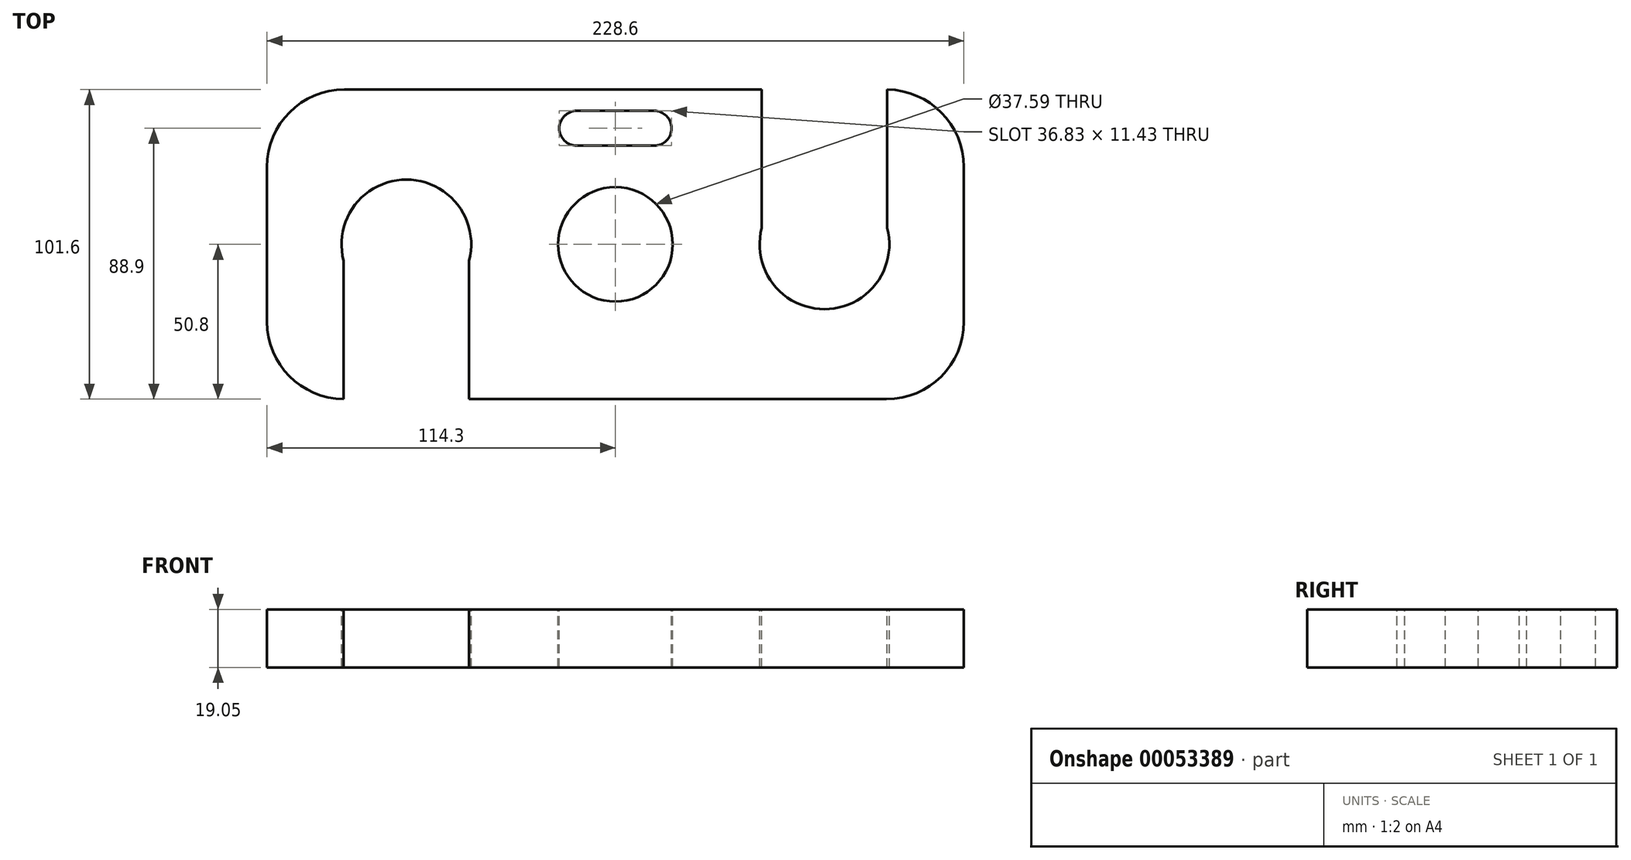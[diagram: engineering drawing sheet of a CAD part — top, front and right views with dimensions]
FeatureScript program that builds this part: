
annotation { "Feature Type Name" : "Feature", "Feature Type Description" : "" }
export const myFeature = defineFeature(function(context is Context, id is Id, definition is map)
    precondition{}
    {
        {
            var Q0;
            Q0=qCreatedBy(makeId("Top.planeOp"),FACE);
            var sketch = newSketch(context, id + "F0", { "sketchPlane" : qUnion([Q0])});
            skLineSegment(sketch, "E0.rect.bottom", {"start": v(88.9, 50.8) * mm, "end": v(-88.9, 50.8) * mm});
            skLineSegment(sketch, "E0.rect.top", {"start": v(88.9, -50.8) * mm, "end": v(-88.9, -50.8) * mm});
            skLineSegment(sketch, "E0.rect.left", {"start": v(114.3, 25.4) * mm, "end": v(114.3, -25.4) * mm});
            skLineSegment(sketch, "E0.rect.right", {"start": v(-114.3, 25.4) * mm, "end": v(-114.3, -25.4) * mm});
            skPoint(sketch, "E0.rect.middle", {"position": v(0, 0) * mm});
            skPoint(sketch, "E1.visualSharp", {"position": v(-114.3, 50.8) * mm});
            skArc(sketch, "E1.filletArc", {"start": v(-88.9, 50.8) * mm, "mid": v(-106.86, 43.36) * mm, "end": v(-114.3, 25.4) * mm});
            skPoint(sketch, "E2.visualSharp", {"position": v(-114.3, -50.8) * mm});
            skArc(sketch, "E2.filletArc", {"start": v(-114.3, -25.4) * mm, "mid": v(-106.86, -43.36) * mm, "end": v(-88.9, -50.8) * mm});
            skPoint(sketch, "E3.visualSharp", {"position": v(114.3, -50.8) * mm});
            skArc(sketch, "E3.filletArc", {"start": v(88.9, -50.8) * mm, "mid": v(106.86, -43.36) * mm, "end": v(114.3, -25.4) * mm});
            skPoint(sketch, "E4.visualSharp", {"position": v(114.3, 50.8) * mm});
            skArc(sketch, "E4.filletArc", {"start": v(114.3, 25.4) * mm, "mid": v(106.86, 43.36) * mm, "end": v(88.9, 50.8) * mm});
            skSolve(sketch);
        }
        {
            var Q0;
            Q0=makeQuery(id+"F0.imprint","IMPRINT",FACE,{"disambiguationData":[TD([[makeQuery(id+"F0.imprint","IMPRINT",EDGE,{"derivedFrom":sQuery(id+"F0.wireOp",EDGE,"E0.rect.bottom")}),1.0]])]});
            extrude(context, id + "F1", {"entities" : qUnion([Q0]), "depth" : 19.05 * mm});
        }
        {
            var Q0;
            Q0=makeQuery(id+"F1.opExtrude","CAP_FACE",FACE,{"disambiguationData":[OSD([sQuery(id+"F0.wireOp",EDGE,"E0.rect.bottom"),sQuery(id+"F0.wireOp",EDGE,"E0.rect.top"),sQuery(id+"F0.wireOp",EDGE,"E0.rect.left"),sQuery(id+"F0.wireOp",EDGE,"E0.rect.right"),sQuery(id+"F0.wireOp",EDGE,"E1.filletArc"),sQuery(id+"F0.wireOp",EDGE,"E2.filletArc"),sQuery(id+"F0.wireOp",EDGE,"E3.filletArc"),sQuery(id+"F0.wireOp",EDGE,"E4.filletArc")])],"isStart":false});
            var sketch = newSketch(context, id + "F2", { "sketchPlane" : qUnion([Q0])});
            skCircle(sketch, "E5", {"center": v(0, 0) * mm, "radius": 18.8 * mm});
            skSolve(sketch);
        }
        {
            var Q0;
            Q0=qSketchRegion(id+"F2",true);
            extrude(context, id + "F3", {"entities" : qUnion([Q0]), "operationType" : NewBodyOperationType.REMOVE, "endBound" : BoundingType.THROUGH_ALL, "oppositeDirection" : true, "depth" : 25.4 * mm});
        }
        {
            var Q0;
            Q0=makeQuery(id+"F1.opExtrude","CAP_FACE",FACE,{"disambiguationData":[OSD([sQuery(id+"F0.wireOp",EDGE,"E0.rect.bottom"),sQuery(id+"F0.wireOp",EDGE,"E0.rect.top"),sQuery(id+"F0.wireOp",EDGE,"E0.rect.left"),sQuery(id+"F0.wireOp",EDGE,"E0.rect.right"),sQuery(id+"F0.wireOp",EDGE,"E1.filletArc"),sQuery(id+"F0.wireOp",EDGE,"E2.filletArc"),sQuery(id+"F0.wireOp",EDGE,"E3.filletArc"),sQuery(id+"F0.wireOp",EDGE,"E4.filletArc")])],"isStart":false});
            var sketch = newSketch(context, id + "F4", { "sketchPlane" : qUnion([Q0])});
            skArc(sketch, "E6", {"start": v(-48, -5.4) * mm, "mid": v(-68.58, 21.27) * mm, "end": v(-89.15, -5.4) * mm});
            skArc(sketch, "E7.MirrorC", {"start": v(89.15, 5.4) * mm, "mid": v(68.58, -21.27) * mm, "end": v(48, 5.4) * mm});
            skLineSegment(sketch, "E8", {"start": v(-89.15, -50.8) * mm, "end": v(-89.15, -5.4) * mm});
            skLineSegment(sketch, "E9", {"start": v(-48, -50.8) * mm, "end": v(-48, -5.4) * mm});
            skLineSegment(sketch, "E10", {"start": v(89.15, 50.8) * mm, "end": v(89.15, 5.4) * mm});
            skLineSegment(sketch, "E11", {"start": v(48, 50.8) * mm, "end": v(48, 5.4) * mm});
            skLineSegment(sketch, "E12", {"start": v(-89.15, -50.8) * mm, "end": v(-48, -50.8) * mm});
            skLineSegment(sketch, "E13", {"start": v(48, 50.8) * mm, "end": v(89.15, 50.8) * mm});
            skLineSegment(sketch, "E14", {"start": v(-89.15, -5.4) * mm, "end": v(-48, -5.4) * mm, "construction": true});
            skLineSegment(sketch, "E15", {"start": v(48, 5.4) * mm, "end": v(89.15, 5.4) * mm, "construction": true});
            skSolve(sketch);
        }
        {
            var Q0;
            Q0=qSketchRegion(id+"F4",true);
            extrude(context, id + "F5", {"entities" : qUnion([Q0]), "operationType" : NewBodyOperationType.REMOVE, "endBound" : BoundingType.THROUGH_ALL, "oppositeDirection" : true, "depth" : 25.4 * mm});
        }
        {
            var Q0;
            Q0=makeQuery(id+"F1.opExtrude","CAP_FACE",FACE,{"disambiguationData":[OSD([sQuery(id+"F0.wireOp",EDGE,"E0.rect.bottom"),sQuery(id+"F0.wireOp",EDGE,"E0.rect.top"),sQuery(id+"F0.wireOp",EDGE,"E0.rect.left"),sQuery(id+"F0.wireOp",EDGE,"E0.rect.right"),sQuery(id+"F0.wireOp",EDGE,"E1.filletArc"),sQuery(id+"F0.wireOp",EDGE,"E2.filletArc"),sQuery(id+"F0.wireOp",EDGE,"E3.filletArc"),sQuery(id+"F0.wireOp",EDGE,"E4.filletArc")])],"isStart":false});
            var sketch = newSketch(context, id + "F6", { "sketchPlane" : qUnion([Q0])});
            skLineSegment(sketch, "E16", {"start": v(-12.7, 38.1) * mm, "end": v(12.7, 38.1) * mm, "construction": true});
            skArc(sketch, "E17.0.startCap", {"start": v(-12.7, 32.39) * mm, "mid": v(-18.42, 38.1) * mm, "end": v(-12.7, 43.81) * mm});
            skArc(sketch, "E17.0.endCap", {"start": v(12.7, 43.81) * mm, "mid": v(18.42, 38.1) * mm, "end": v(12.7, 32.39) * mm});
            skLineSegment(sketch, "E17.0.left", {"start": v(-12.7, 43.81) * mm, "end": v(12.7, 43.82) * mm});
            skLineSegment(sketch, "E17.0.right", {"start": v(-12.7, 32.39) * mm, "end": v(12.7, 32.39) * mm});
            skSolve(sketch);
        }
        {
            var Q0;
            Q0 = qSketchRegion(id + "F6", true);
            extrude(context, id + "F7", {"entities" : qUnion([Q0]), "operationType" : NewBodyOperationType.REMOVE, "endBound" : BoundingType.THROUGH_ALL, "oppositeDirection" : true, "depth" : 25.4 * mm});
        }
    });
